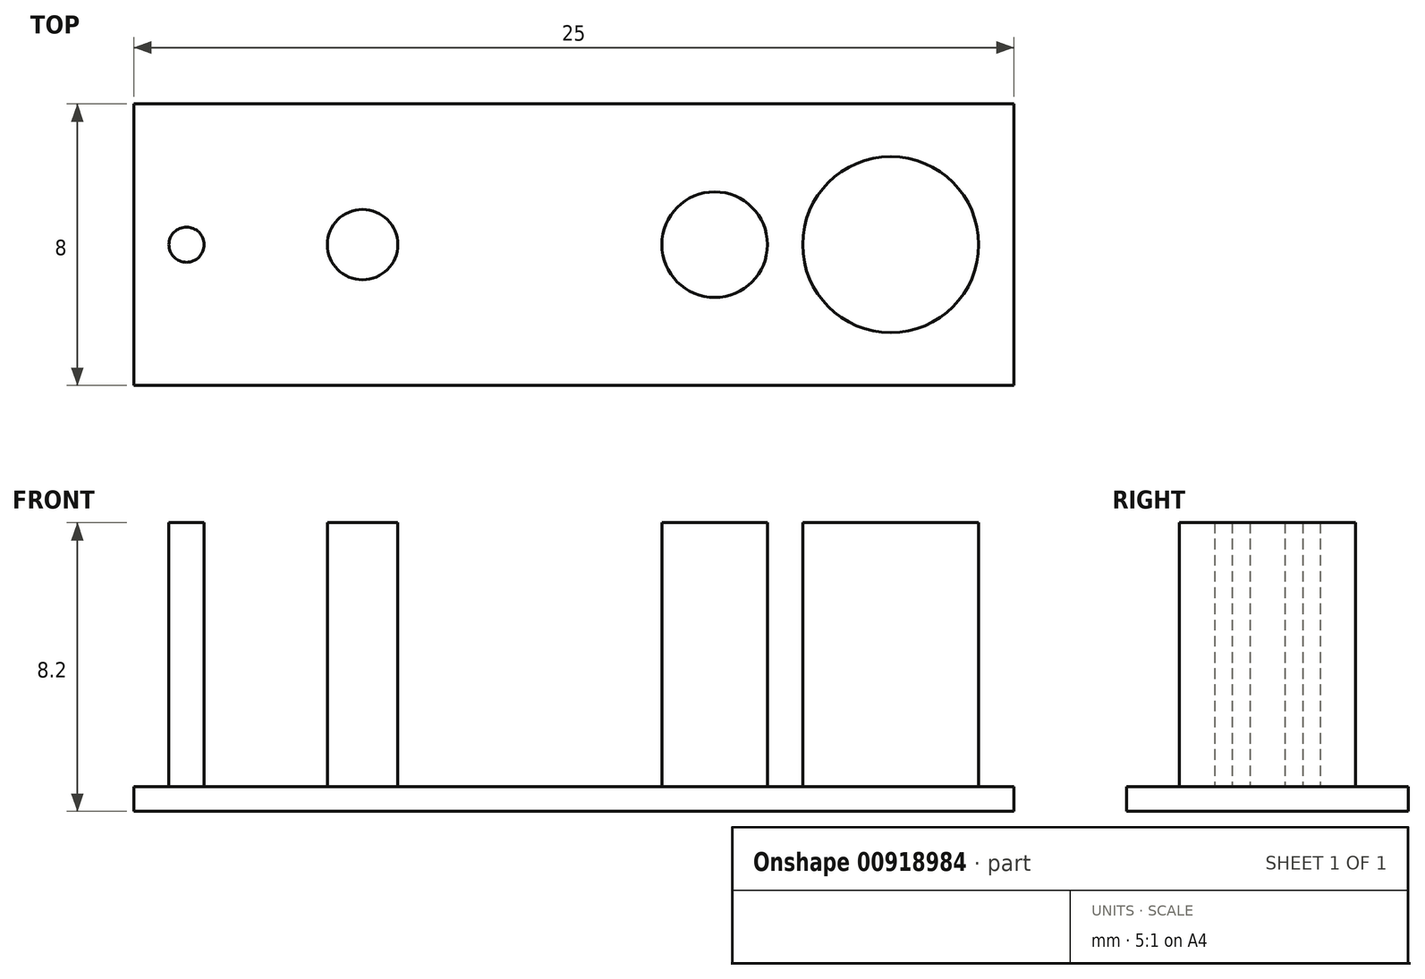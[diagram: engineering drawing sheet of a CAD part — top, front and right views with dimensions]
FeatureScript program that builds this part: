
annotation { "Feature Type Name" : "Feature", "Feature Type Description" : "" }
export const myFeature = defineFeature(function(context is Context, id is Id, definition is map)
    precondition{}
    {
        {
            var Q0;
            Q0=qCreatedBy(makeId("Top.planeOp"),FACE);
            var sketch = newSketch(context, id + "F0", { "sketchPlane" : qUnion([Q0])});
            skCircle(sketch, "E0", {"center": v(-5, 0) * mm, "radius": 1 * mm});
            skCircle(sketch, "E1", {"center": v(5, 0) * mm, "radius": 1.5 * mm});
            skCircle(sketch, "E2", {"center": v(-10, 0) * mm, "radius": 0.5 * mm});
            skCircle(sketch, "E3", {"center": v(10, 0) * mm, "radius": 2.5 * mm});
            skSolve(sketch);
        }
        {
            var Q0;
            Q0 = qSketchRegion(id + "F0", true);
            extrude(context, id + "F1", {"entities" : qUnion([Q0]), "depth" : 7.5 * mm, "offsetDistance" : 25 * mm});
        }
        {
            var Q0;
            Q0=qCreatedBy(makeId("Top.planeOp"),FACE);
            var sketch = newSketch(context, id + "F2", { "sketchPlane" : qUnion([Q0])});
            skLineSegment(sketch, "E4.bottom", {"start": v(-11.5, -4) * mm, "end": v(13.5, -4) * mm});
            skLineSegment(sketch, "E4.top", {"start": v(-11.5, 4) * mm, "end": v(13.5, 4) * mm});
            skLineSegment(sketch, "E4.left", {"start": v(-11.5, -4) * mm, "end": v(-11.5, 4) * mm});
            skLineSegment(sketch, "E4.right", {"start": v(13.5, -4) * mm, "end": v(13.5, 4) * mm});
            skSolve(sketch);
        }
        {
            var Q0;
            Q0=makeQuery(id+"F2.imprint","IMPRINT",FACE,{"disambiguationData":[TD([[makeQuery(id+"F2.imprint","IMPRINT",EDGE,{"derivedFrom":sQuery(id+"F2.wireOp",EDGE,"E4.bottom")}),1.0]])]});
            extrude(context, id + "F3", {"entities" : qUnion([Q0]), "oppositeDirection" : true, "depth" : 0.7 * mm, "offsetDistance" : 25 * mm});
        }
    });
